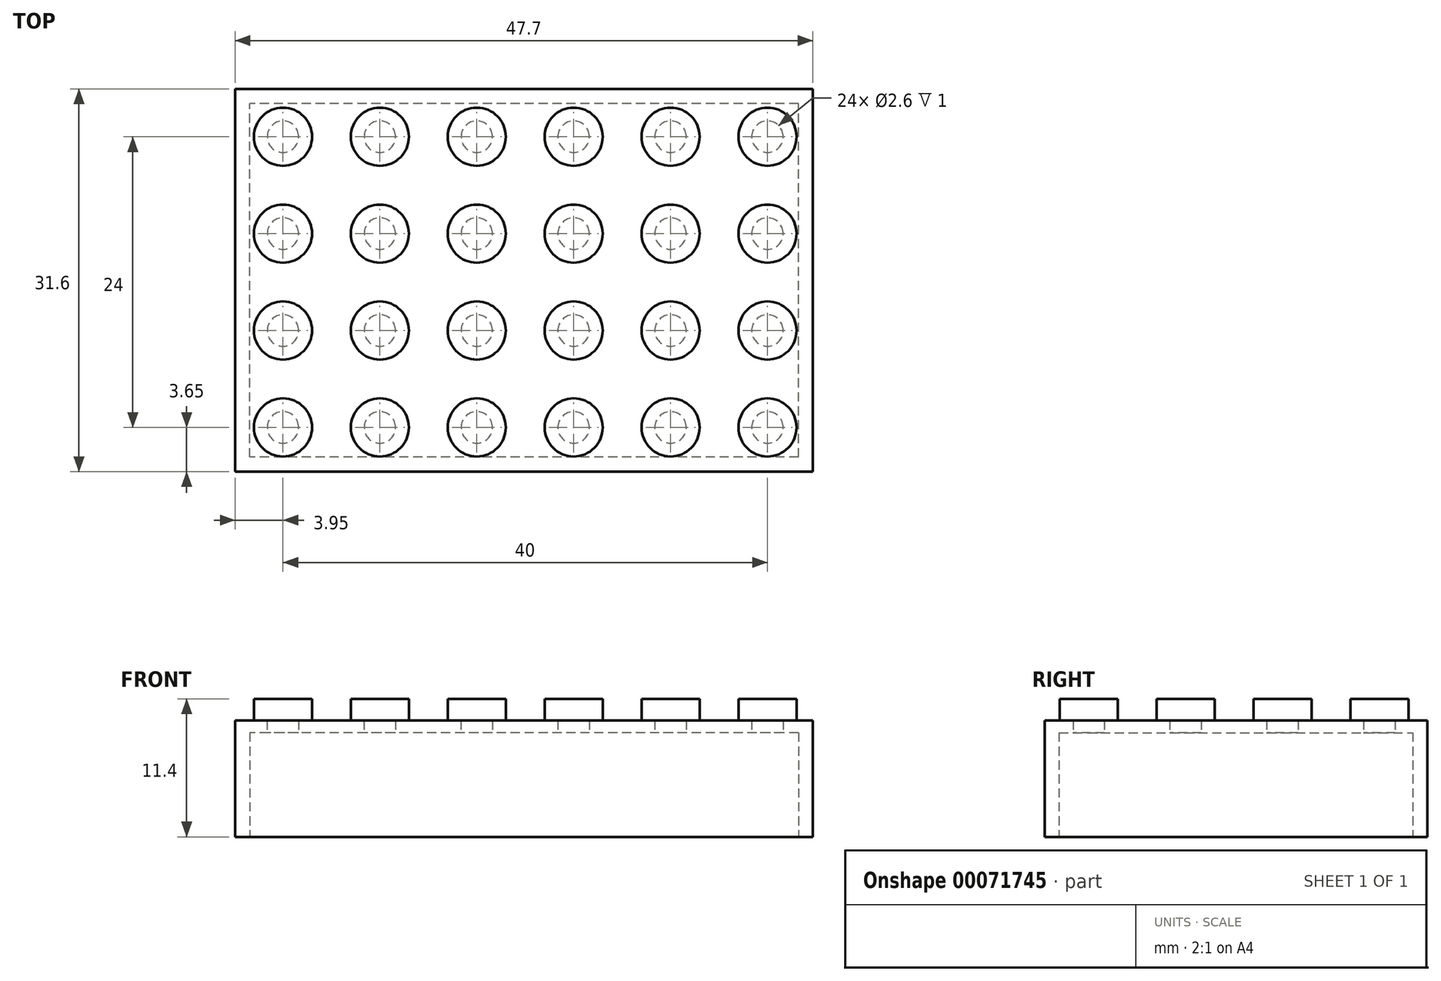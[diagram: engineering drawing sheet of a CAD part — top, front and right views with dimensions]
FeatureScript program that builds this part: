
annotation { "Feature Type Name" : "Feature", "Feature Type Description" : "" }
export const myFeature = defineFeature(function(context is Context, id is Id, definition is map)
    precondition{}
    {
        {
            var Q0;
            Q0=qCreatedBy(makeId("Top.planeOp"),FACE);
            var sketch = newSketch(context, id + "F0", { "sketchPlane" : qUnion([Q0])});
            skLineSegment(sketch, "E0.rect.bottom", {"start": v(23.85, 15.8) * mm, "end": v(-23.85, 15.8) * mm});
            skLineSegment(sketch, "E0.rect.top", {"start": v(23.85, -15.8) * mm, "end": v(-23.85, -15.8) * mm});
            skLineSegment(sketch, "E0.rect.left", {"start": v(23.85, 15.8) * mm, "end": v(23.85, -15.8) * mm});
            skLineSegment(sketch, "E0.rect.right", {"start": v(-23.85, 15.8) * mm, "end": v(-23.85, -15.8) * mm});
            skPoint(sketch, "E0.rect.middle", {"position": v(0, 0) * mm});
            skSolve(sketch);
        }
        {
            var Q0;
            Q0 = qSketchRegion(id + "F0", true);
            extrude(context, id + "F1", {"entities" : qUnion([Q0]), "depth" : 9.6 * mm});
        }
        {
            var Q0;
            Q0=makeQuery(id+"F0.imprint","IMPRINT",FACE,{"disambiguationData":[TD([[makeQuery(id+"F0.imprint","IMPRINT",EDGE,{"derivedFrom":sQuery(id+"F0.wireOp",EDGE,"E0.rect.bottom")}),1.0]])]});
            var sketch = newSketch(context, id + "F2", { "sketchPlane" : qUnion([Q0])});
            skLineSegment(sketch, "E1.rect.bottom", {"start": v(22.65, -14.6) * mm, "end": v(-22.65, -14.6) * mm});
            skLineSegment(sketch, "E1.rect.top", {"start": v(22.65, 14.6) * mm, "end": v(-22.65, 14.6) * mm});
            skLineSegment(sketch, "E1.rect.left", {"start": v(22.65, -14.6) * mm, "end": v(22.65, 14.6) * mm});
            skLineSegment(sketch, "E1.rect.right", {"start": v(-22.65, -14.6) * mm, "end": v(-22.65, 14.6) * mm});
            skPoint(sketch, "E1.rect.middle", {"position": v(0, 0) * mm});
            skSolve(sketch);
        }
        {
            var Q0;
            Q0=makeQuery(id+"F2.imprint","IMPRINT",FACE,{"disambiguationData":[TD([[makeQuery(id+"F2.imprint","IMPRINT",EDGE,{"derivedFrom":sQuery(id+"F2.wireOp",EDGE,"E1.rect.bottom")}),-1.0]])]});
            extrude(context, id + "F3", {"entities" : qUnion([Q0]), "operationType" : NewBodyOperationType.REMOVE, "depth" : 8.6 * mm});
        }
        {
            var Q0;
            Q0=makeQuery(id+"F1.opExtrude","CAP_FACE",FACE,{"disambiguationData":[OSD([sQuery(id+"F0.wireOp",EDGE,"E0.rect.bottom"),sQuery(id+"F0.wireOp",EDGE,"E0.rect.top"),sQuery(id+"F0.wireOp",EDGE,"E0.rect.left"),sQuery(id+"F0.wireOp",EDGE,"E0.rect.right")])],"isStart":false});
            var sketch = newSketch(context, id + "F4", { "sketchPlane" : qUnion([Q0])});
            skCircle(sketch, "E2", {"center": v(-19.9, 11.85) * mm, "radius": 2.4 * mm});
            skCircle(sketch, "E3.0.1.0", {"center": v(-19.9, 3.85) * mm, "radius": 2.4 * mm});
            skCircle(sketch, "E3.0.2.0", {"center": v(-19.9, -4.15) * mm, "radius": 2.4 * mm});
            skCircle(sketch, "E3.0.3.0", {"center": v(-19.9, -12.15) * mm, "radius": 2.4 * mm});
            skCircle(sketch, "E3.1.0.0", {"center": v(-11.9, 11.85) * mm, "radius": 2.4 * mm});
            skCircle(sketch, "E3.1.1.0", {"center": v(-11.9, 3.85) * mm, "radius": 2.4 * mm});
            skCircle(sketch, "E3.1.2.0", {"center": v(-11.9, -4.15) * mm, "radius": 2.4 * mm});
            skCircle(sketch, "E3.1.3.0", {"center": v(-11.9, -12.15) * mm, "radius": 2.4 * mm});
            skCircle(sketch, "E3.2.0.0", {"center": v(-3.9, 11.85) * mm, "radius": 2.4 * mm});
            skCircle(sketch, "E3.2.1.0", {"center": v(-3.9, 3.85) * mm, "radius": 2.4 * mm});
            skCircle(sketch, "E3.2.2.0", {"center": v(-3.9, -4.15) * mm, "radius": 2.4 * mm});
            skCircle(sketch, "E3.2.3.0", {"center": v(-3.9, -12.15) * mm, "radius": 2.4 * mm});
            skCircle(sketch, "E3.3.0.0", {"center": v(4.1, 11.85) * mm, "radius": 2.4 * mm});
            skCircle(sketch, "E3.3.1.0", {"center": v(4.1, 3.85) * mm, "radius": 2.4 * mm});
            skCircle(sketch, "E3.3.2.0", {"center": v(4.1, -4.15) * mm, "radius": 2.4 * mm});
            skCircle(sketch, "E3.3.3.0", {"center": v(4.1, -12.15) * mm, "radius": 2.4 * mm});
            skCircle(sketch, "E3.4.0.0", {"center": v(12.1, 11.85) * mm, "radius": 2.4 * mm});
            skCircle(sketch, "E3.4.1.0", {"center": v(12.1, 3.85) * mm, "radius": 2.4 * mm});
            skCircle(sketch, "E3.4.2.0", {"center": v(12.1, -4.15) * mm, "radius": 2.4 * mm});
            skCircle(sketch, "E3.4.3.0", {"center": v(12.1, -12.15) * mm, "radius": 2.4 * mm});
            skCircle(sketch, "E3.5.0.0", {"center": v(20.1, 11.85) * mm, "radius": 2.4 * mm});
            skCircle(sketch, "E3.5.1.0", {"center": v(20.1, 3.85) * mm, "radius": 2.4 * mm});
            skCircle(sketch, "E3.5.2.0", {"center": v(20.1, -4.15) * mm, "radius": 2.4 * mm});
            skCircle(sketch, "E3.5.3.0", {"center": v(20.1, -12.15) * mm, "radius": 2.4 * mm});
            skLineSegment(sketch, "E3.direction1", {"start": v(-19.9, 11.85) * mm, "end": v(-11.9, 11.85) * mm, "construction": true});
            skLineSegment(sketch, "E3.direction2", {"start": v(-19.9, 11.85) * mm, "end": v(-19.9, 3.85) * mm, "construction": true});
            skSolve(sketch);
        }
        {
            var Q0;
            Q0 = qSketchRegion(id + "F4", true);
            extrude(context, id + "F5", {"entities" : qUnion([Q0]), "operationType" : NewBodyOperationType.ADD, "depth" : 1.8 * mm});
        }
        {
            var Q0;
            Q0=makeQuery(id+"F2.imprint","IMPRINT",FACE,{"disambiguationData":[TD([[makeQuery(id+"F2.imprint","IMPRINT",EDGE,{"derivedFrom":sQuery(id+"F2.wireOp",EDGE,"E1.rect.bottom")}),1.0]])]});
            cPlane(context, id + "F6", {"entities" : qUnion([Q0]), "cplaneType" : CPlaneType.OFFSET, "offset" : 8.4 * mm, "width" : 150 * mm, "height" : 150 * mm});
        }
        {
            var Q0;
            Q0=qCreatedBy(id+"F6.planeOp",FACE);
            var sketch = newSketch(context, id + "F7", { "sketchPlane" : qUnion([Q0])});
            skCircle(sketch, "E4", {"center": v(-19.9, -12.15) * mm, "radius": 1.3 * mm});
            skCircle(sketch, "E5.0.1.0", {"center": v(-19.9, -4.15) * mm, "radius": 1.3 * mm});
            skCircle(sketch, "E5.0.2.0", {"center": v(-19.9, 3.85) * mm, "radius": 1.3 * mm});
            skCircle(sketch, "E5.0.3.0", {"center": v(-19.9, 11.85) * mm, "radius": 1.3 * mm});
            skCircle(sketch, "E5.1.0.0", {"center": v(-11.9, -12.15) * mm, "radius": 1.3 * mm});
            skCircle(sketch, "E5.1.1.0", {"center": v(-11.9, -4.15) * mm, "radius": 1.3 * mm});
            skCircle(sketch, "E5.1.2.0", {"center": v(-11.9, 3.85) * mm, "radius": 1.3 * mm});
            skCircle(sketch, "E5.1.3.0", {"center": v(-11.9, 11.85) * mm, "radius": 1.3 * mm});
            skCircle(sketch, "E5.2.0.0", {"center": v(-3.9, -12.15) * mm, "radius": 1.3 * mm});
            skCircle(sketch, "E5.2.1.0", {"center": v(-3.9, -4.15) * mm, "radius": 1.3 * mm});
            skCircle(sketch, "E5.2.2.0", {"center": v(-3.9, 3.85) * mm, "radius": 1.3 * mm});
            skCircle(sketch, "E5.2.3.0", {"center": v(-3.9, 11.85) * mm, "radius": 1.3 * mm});
            skCircle(sketch, "E5.3.0.0", {"center": v(4.1, -12.15) * mm, "radius": 1.3 * mm});
            skCircle(sketch, "E5.3.1.0", {"center": v(4.1, -4.15) * mm, "radius": 1.3 * mm});
            skCircle(sketch, "E5.3.2.0", {"center": v(4.1, 3.85) * mm, "radius": 1.3 * mm});
            skCircle(sketch, "E5.3.3.0", {"center": v(4.1, 11.85) * mm, "radius": 1.3 * mm});
            skCircle(sketch, "E5.4.0.0", {"center": v(12.1, -12.15) * mm, "radius": 1.3 * mm});
            skCircle(sketch, "E5.4.1.0", {"center": v(12.1, -4.15) * mm, "radius": 1.3 * mm});
            skCircle(sketch, "E5.4.2.0", {"center": v(12.1, 3.85) * mm, "radius": 1.3 * mm});
            skCircle(sketch, "E5.4.3.0", {"center": v(12.1, 11.85) * mm, "radius": 1.3 * mm});
            skCircle(sketch, "E5.5.0.0", {"center": v(20.1, -12.15) * mm, "radius": 1.3 * mm});
            skCircle(sketch, "E5.5.1.0", {"center": v(20.1, -4.15) * mm, "radius": 1.3 * mm});
            skCircle(sketch, "E5.5.2.0", {"center": v(20.1, 3.85) * mm, "radius": 1.3 * mm});
            skCircle(sketch, "E5.5.3.0", {"center": v(20.1, 11.85) * mm, "radius": 1.3 * mm});
            skLineSegment(sketch, "E5.direction1", {"start": v(-19.9, -12.15) * mm, "end": v(-11.9, -12.15) * mm, "construction": true});
            skLineSegment(sketch, "E5.direction2", {"start": v(-19.9, -12.15) * mm, "end": v(-19.9, -4.15) * mm, "construction": true});
            skSolve(sketch);
        }
        {
            var Q0;
            Q0 = qSketchRegion(id + "F7", true);
            extrude(context, id + "F8", {"entities" : qUnion([Q0]), "operationType" : NewBodyOperationType.REMOVE, "depth" : 1.2 * mm});
        }
    });
